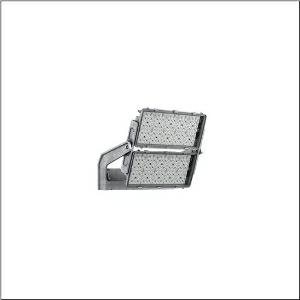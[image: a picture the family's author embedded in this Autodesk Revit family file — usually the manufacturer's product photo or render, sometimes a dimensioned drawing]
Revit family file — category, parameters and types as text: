
# Revit family: floodlight_fl_11_maxi___rs08_5xa779114l01ba_dd38
name_source: partatom
category: Lighting Fixtures
units: mm (PartAtom-declared; Revit-internal decimal feet)

## family parameters
Cut with Voids When Loaded = No
Host = Face
Light Source = No
Part Type = Normal
Room Calculation Point = No
Round Connector Dimension = Use Diameter
Shared = No

## types (1)
- --- (1 x LED, 74500 lm, 707.9 W, 5700K)
    Apparent Load = 708 VA
    CIE Flux Codes = 70 87 98 100 100
    Color Rendering = 90
    Color Temperature = 5700K
    Default Elevation = 1800 mm
    Description = Floodlight FL 11  maxi floodlight; light control with lens of PMMA; cover panel of toughened safety glass, transparent; light distribution: RS08, rotationally symmetric direct distribution, LEDcolour temperature: 5700K, rated luminous flux: 75.300lm, colour rendering: CRI > 90, light colour: 957; luminous efficacy: 106lm/W; brightness control: DALI 2 (1 DALI address); with terminal, 5-pole, max. 2.5mm², mains connection: 220..240V/380..400V AC, 50/60Hz, surge voltage resistance: line to ground: 10kV, dustproof LED module, LED unit replaceable without ESD environment, ECG replaceable separately, dimming range 10..100%; 708W floodlight with 2x LED unit of diecast aluminium, coated grey; length: 713mm / width: 651mm / height: 338mm; housing frame, of diecast aluminium, uncoated, natural, mounting bracket, of diecast aluminium, uncoated, natural, equipment: Longlife, protection rating (complete): IP66; insulation class (complete): insulation class I (protective earthing); certification: CE, ENEC, VDE; ball protection: ball impact resistant, only for outdoor installations, rated ambient temperature 10°C, permissible operating ambient temperature: -40..+30°C, permissible storage temperature: -40..+85°C; packaging unit: 1 piece

Light Distribution: RS08
    Height = 320 mm
    Lamp = 1 x LED
    Lamp Light Flux = 74500 lm
    Lamp Power = 707.9 W
    Lamp count = 1
    Length = 712 mm
    Luminous efficacy = 105 lm/W
    Manufacturer = Siteco
    ModVariant = No
    Model = 5XA779114L01BA
    Number of Poles = 1
    OnlyDefault = Yes
    Power Factor = 1
    Product Name = Floodlight FL 11 maxi | RS08
    Product group = floodlight | pylon top
    ProductGroupID = 6101
    Protection Class = Protection class I
    Protection Degree = IP 66
    RLX_Detail_Level = 1
    RlxData = <blob elided: 41981 chars, md5=2a33af50>
    Socket = socket
    Standby Power = 0 W
    System Light Flux = 74500 lm
    System Power = 708 W
    Type Comments = factory setting: luminous flux: 100 % | dim-lin: 254 | 740 mA
    Type Image = l_1006932.jpg
    URL = http://relux.com
    VarID = @adj_060463
    Voltage = 0 V
    Weight = 0.00 kg
    Width = 655 mm

## geometry (parser evidence)
native form markers: Blend x4, Sweep x11
no freeform markers — native parametric forms only
